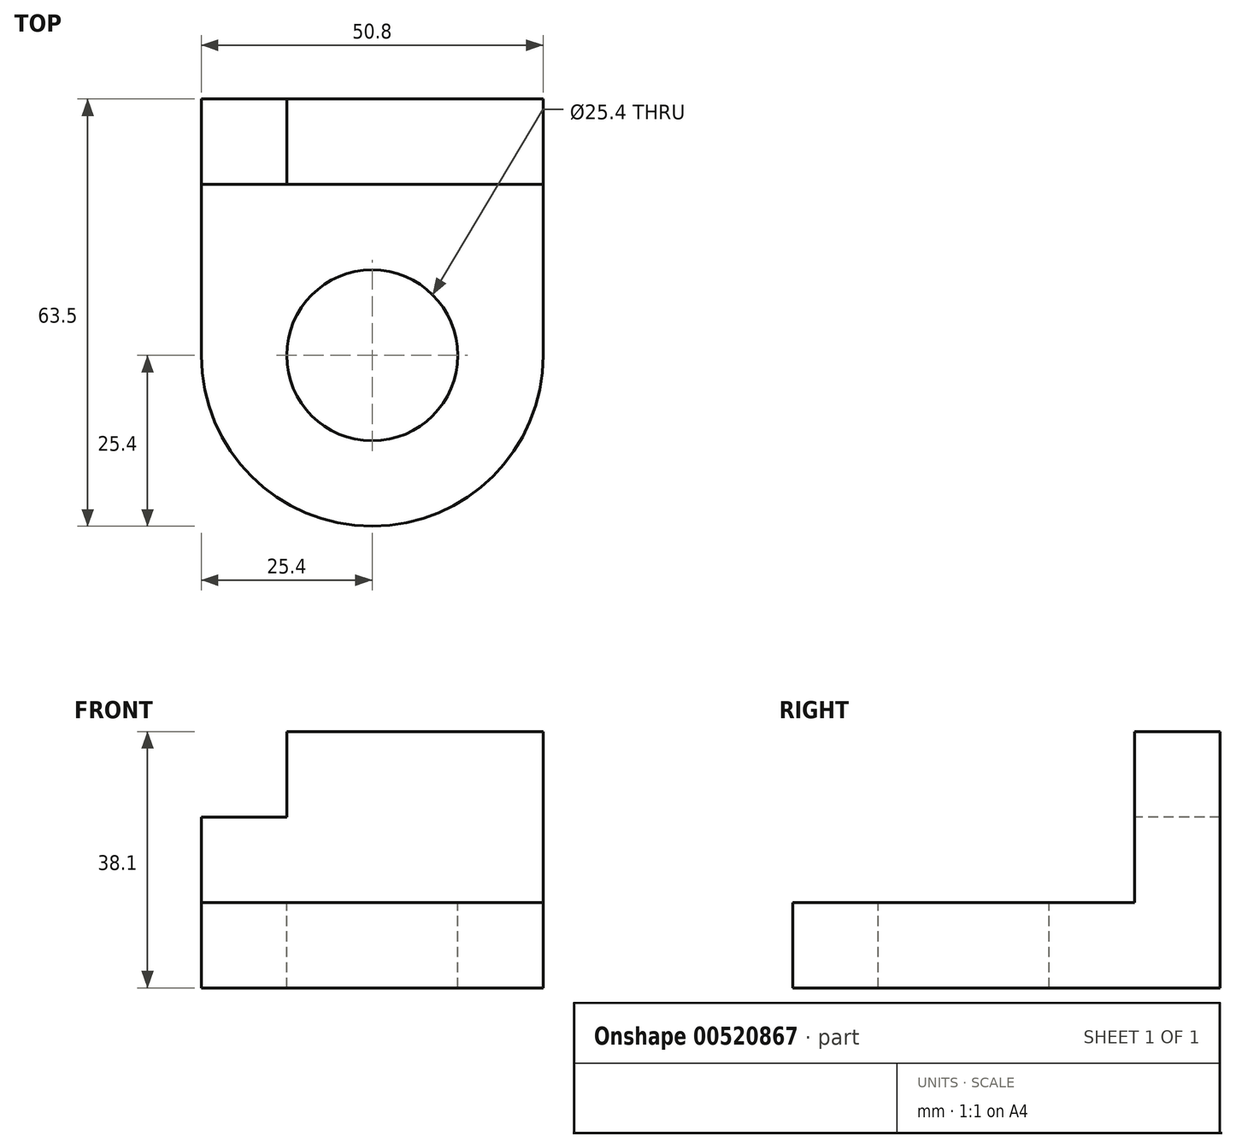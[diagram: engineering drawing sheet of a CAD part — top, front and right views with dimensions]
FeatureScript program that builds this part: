
annotation { "Feature Type Name" : "Feature", "Feature Type Description" : "" }
export const myFeature = defineFeature(function(context is Context, id is Id, definition is map)
    precondition{}
    {
        {
            var Q0;
            Q0=qCreatedBy(makeId("Front.planeOp"),FACE);
            var sketch = newSketch(context, id + "F0", { "sketchPlane" : qUnion([Q0])});
            skLineSegment(sketch, "E0.bottom", {"start": v(-25.4, 0) * mm, "end": v(25.4, 0) * mm});
            skLineSegment(sketch, "E0.top", {"start": v(-25.4, 25.4) * mm, "end": v(25.4, 25.4) * mm});
            skLineSegment(sketch, "E0.left", {"start": v(-25.4, 0) * mm, "end": v(-25.4, 25.4) * mm});
            skLineSegment(sketch, "E0.right", {"start": v(25.4, 0) * mm, "end": v(25.4, 25.4) * mm});
            skLineSegment(sketch, "E1.bottom", {"start": v(-12.7, 25.4) * mm, "end": v(25.4, 25.4) * mm});
            skLineSegment(sketch, "E1.top", {"start": v(-12.7, 38.1) * mm, "end": v(25.4, 38.1) * mm});
            skLineSegment(sketch, "E1.left", {"start": v(-12.7, 25.4) * mm, "end": v(-12.7, 38.1) * mm});
            skLineSegment(sketch, "E1.right", {"start": v(25.4, 25.4) * mm, "end": v(25.4, 38.1) * mm});
            skSolve(sketch);
        }
        {
            var Q0;
            Q0 = qSketchRegion(id + "F0", true);
            extrude(context, id + "F1", {"entities" : qUnion([Q0]), "oppositeDirection" : true, "depth" : 12.7 * mm, "offsetDistance" : 25.4 * mm});
        }
        {
            var Q0;
            Q0=makeQuery(id+"F1.opExtrude","CAP_FACE",FACE,{"disambiguationData":[OSD([sQuery(id+"F0.wireOp",EDGE,"E0.bottom"),sQuery(id+"F0.wireOp",EDGE,"E0.top"),sQuery(id+"F0.wireOp",EDGE,"E0.left"),sQuery(id+"F0.wireOp",EDGE,"E0.right"),sQuery(id+"F0.wireOp",EDGE,"E1.top"),sQuery(id+"F0.wireOp",EDGE,"E1.left"),sQuery(id+"F0.wireOp",EDGE,"E1.right")])],"isStart":true});
            var sketch = newSketch(context, id + "F2", { "sketchPlane" : qUnion([Q0])});
            skLineSegment(sketch, "E2.bottom", {"start": v(-25.4, 0) * mm, "end": v(25.4, 0) * mm});
            skLineSegment(sketch, "E2.top", {"start": v(-25.4, 12.7) * mm, "end": v(25.4, 12.7) * mm});
            skLineSegment(sketch, "E2.left", {"start": v(-25.4, 0) * mm, "end": v(-25.4, 12.7) * mm});
            skLineSegment(sketch, "E2.right", {"start": v(25.4, 0) * mm, "end": v(25.4, 12.7) * mm});
            skSolve(sketch);
        }
        {
            var Q0;
            Q0 = qSketchRegion(id + "F2", true);
            extrude(context, id + "F3", {"entities" : qUnion([Q0]), "operationType" : NewBodyOperationType.ADD, "depth" : 50.8 * mm, "offsetDistance" : 25.4 * mm});
        }
        {
            var Q0;
            Q0=makeQuery(id+"F3.opExtrude","SWEPT_FACE",FACE,{"disambiguationData":[OSD([sQuery(id+"F2.wireOp",EDGE,"E2.top")])]});
            var sketch = newSketch(context, id + "F4", { "sketchPlane" : qUnion([Q0])});
            skCircle(sketch, "E3", {"center": v(0, -25.4) * mm, "radius": 12.7 * mm});
            skSolve(sketch);
        }
        {
            var Q0;
            Q0=makeQuery(id+"F4.imprint","IMPRINT",FACE,{"disambiguationData":[TD([[makeQuery(id+"F4.imprint","IMPRINT",EDGE,{"derivedFrom":sQuery(id+"F4.wireOp",EDGE,"E3")}),1.0]])]});
            extrude(context, id + "F5", {"entities" : qUnion([Q0]), "operationType" : NewBodyOperationType.REMOVE, "endBound" : BoundingType.THROUGH_ALL, "oppositeDirection" : true, "depth" : 25.4 * mm, "offsetDistance" : 25.4 * mm});
        }
        {
            var Q0;
            Q0=makeQuery(id+"F3.opExtrude","CAP_EDGE",EDGE,{"disambiguationData":[OSD([sQuery(id+"F2.wireOp",EDGE,"E2.left")])],"isStart":false});
            var Q1;
            Q1=makeQuery(id+"F3.opExtrude","CAP_EDGE",EDGE,{"disambiguationData":[OSD([sQuery(id+"F2.wireOp",EDGE,"E2.right")])],"isStart":false});
            fillet(context, id + "F6", {"entities" : qUnion([Q0, Q1]), "radius" : 25.4 * mm, "tangentPropagation" : true, "allowEdgeOverflow" : false});
        }
    });
